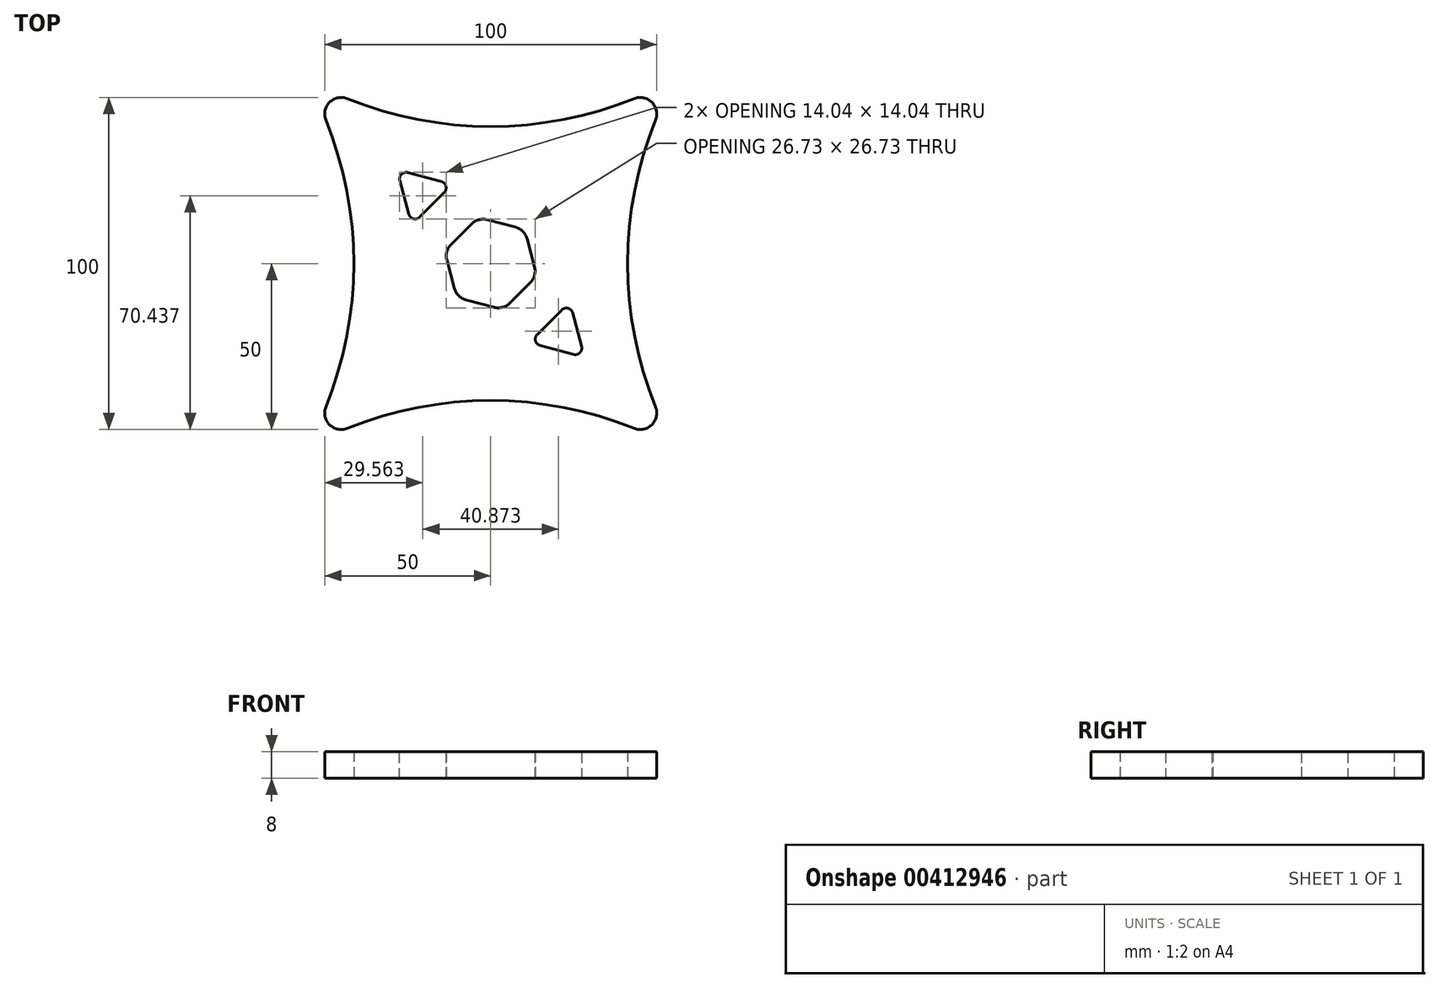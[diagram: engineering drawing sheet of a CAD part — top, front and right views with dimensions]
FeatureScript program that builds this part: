
annotation { "Feature Type Name" : "Feature", "Feature Type Description" : "" }
export const myFeature = defineFeature(function(context is Context, id is Id, definition is map)
    precondition{}
    {
        {
            var Q0;
            Q0=qCreatedBy(makeId("Top.planeOp"),FACE);
            var sketch = newSketch(context, id + "F0", { "sketchPlane" : qUnion([Q0])});
            skLineSegment(sketch, "E0.bottom", {"start": v(55.55, -55.55) * mm, "end": v(-55.55, -55.55) * mm, "construction": true});
            skLineSegment(sketch, "E0.top", {"start": v(55.55, 55.55) * mm, "end": v(-55.55, 55.55) * mm, "construction": true});
            skLineSegment(sketch, "E0.left", {"start": v(55.55, -55.55) * mm, "end": v(55.55, 55.55) * mm, "construction": true});
            skLineSegment(sketch, "E0.right", {"start": v(-55.55, -55.55) * mm, "end": v(-55.55, 55.55) * mm, "construction": true});
            skArc(sketch, "E1", {"start": v(-43.13, 49.64) * mm, "mid": v(0, 41.24) * mm, "end": v(43.12, 49.64) * mm});
            skArc(sketch, "E2.MirrorCS", {"start": v(-43.13, -49.64) * mm, "mid": v(0, -41.24) * mm, "end": v(43.12, -49.64) * mm});
            skArc(sketch, "E3", {"start": v(-49.64, -43.12) * mm, "mid": v(-41.24, 0) * mm, "end": v(-49.64, 43.12) * mm});
            skArc(sketch, "E4.MirrorCS", {"start": v(49.64, -43.12) * mm, "mid": v(41.24, 0) * mm, "end": v(49.64, 43.12) * mm});
            skPoint(sketch, "E5.visualSharp", {"position": v(-55.55, 55.55) * mm});
            skArc(sketch, "E5.filletArc", {"start": v(-43.12, 49.64) * mm, "mid": v(-48.54, 48.54) * mm, "end": v(-49.64, 43.12) * mm});
            skPoint(sketch, "E6.visualSharp", {"position": v(55.55, 55.55) * mm});
            skArc(sketch, "E6.filletArc", {"start": v(49.64, 43.12) * mm, "mid": v(48.54, 48.54) * mm, "end": v(43.12, 49.64) * mm});
            skPoint(sketch, "E7.visualSharp", {"position": v(55.55, -55.55) * mm});
            skArc(sketch, "E7.filletArc", {"start": v(43.12, -49.64) * mm, "mid": v(48.54, -48.54) * mm, "end": v(49.64, -43.12) * mm});
            skPoint(sketch, "E8.visualSharp", {"position": v(-55.55, -55.55) * mm});
            skArc(sketch, "E8.filletArc", {"start": v(-49.64, -43.12) * mm, "mid": v(-48.54, -48.54) * mm, "end": v(-43.12, -49.64) * mm});
            skLineSegment(sketch, "E9", {"start": v(55.55, 55.55) * mm, "end": v(-55.55, -55.55) * mm, "construction": true});
            skLineSegment(sketch, "E10", {"start": v(-55.55, 55.55) * mm, "end": v(55.55, -55.55) * mm, "construction": true});
            skCircle(sketch, "E11.cCircle", {"center": v(0, 0) * mm, "radius": 12.5 * mm, "construction": true});
            skLineSegment(sketch, "E11.0", {"start": v(11.9, -5.78) * mm, "end": v(5.78, -11.9) * mm});
            skLineSegment(sketch, "E11.1", {"start": v(0.95, -13.2) * mm, "end": v(-7.42, -10.95) * mm});
            skLineSegment(sketch, "E11.2", {"start": v(-10.95, -7.42) * mm, "end": v(-13.2, 0.95) * mm});
            skLineSegment(sketch, "E11.3", {"start": v(-11.9, 5.78) * mm, "end": v(-5.78, 11.9) * mm});
            skLineSegment(sketch, "E11.4", {"start": v(-0.95, 13.2) * mm, "end": v(7.42, 10.95) * mm});
            skLineSegment(sketch, "E11.5", {"start": v(10.95, 7.42) * mm, "end": v(13.2, -0.95) * mm});
            skPoint(sketch, "E11.0.midPoint", {"position": v(8.84, -8.84) * mm});
            skPoint(sketch, "E12.visualSharp", {"position": v(-3.74, 13.94) * mm});
            skArc(sketch, "E12.filletArc", {"start": v(-0.95, 13.2) * mm, "mid": v(-3.54, 13.2) * mm, "end": v(-5.78, 11.9) * mm});
            skPoint(sketch, "E13.visualSharp", {"position": v(-13.94, 3.74) * mm});
            skArc(sketch, "E13.filletArc", {"start": v(-11.9, 5.78) * mm, "mid": v(-13.2, 3.54) * mm, "end": v(-13.2, 0.95) * mm});
            skPoint(sketch, "E14.visualSharp", {"position": v(-10.2, -10.2) * mm});
            skArc(sketch, "E14.filletArc", {"start": v(-10.95, -7.42) * mm, "mid": v(-9.66, -9.66) * mm, "end": v(-7.42, -10.95) * mm});
            skPoint(sketch, "E15.visualSharp", {"position": v(3.74, -13.94) * mm});
            skArc(sketch, "E15.filletArc", {"start": v(0.95, -13.2) * mm, "mid": v(3.54, -13.2) * mm, "end": v(5.78, -11.9) * mm});
            skPoint(sketch, "E16.visualSharp", {"position": v(13.94, -3.74) * mm});
            skArc(sketch, "E16.filletArc", {"start": v(11.9, -5.78) * mm, "mid": v(13.2, -3.54) * mm, "end": v(13.2, -0.95) * mm});
            skPoint(sketch, "E17.visualSharp", {"position": v(10.2, 10.2) * mm});
            skArc(sketch, "E17.filletArc", {"start": v(10.95, 7.42) * mm, "mid": v(9.66, 9.66) * mm, "end": v(7.42, 10.95) * mm});
            skCircle(sketch, "E18.cCircle", {"center": v(-21.21, 21.21) * mm, "radius": 5 * mm, "construction": true});
            skLineSegment(sketch, "E18.0", {"start": v(-11.55, 23.8) * mm, "end": v(-23.8, 11.55) * mm});
            skLineSegment(sketch, "E18.1", {"start": v(-23.8, 11.55) * mm, "end": v(-28.28, 28.28) * mm});
            skLineSegment(sketch, "E18.2", {"start": v(-28.28, 28.28) * mm, "end": v(-11.55, 23.8) * mm});
            skPoint(sketch, "E18.0.midPoint", {"position": v(-17.68, 17.68) * mm});
            skLineSegment(sketch, "E19.MirrorCS", {"start": v(28.28, -28.28) * mm, "end": v(23.8, -11.55) * mm});
            skLineSegment(sketch, "E20.MirrorCS", {"start": v(23.8, -11.55) * mm, "end": v(11.55, -23.8) * mm});
            skLineSegment(sketch, "E21.MirrorCS", {"start": v(11.55, -23.8) * mm, "end": v(28.28, -28.28) * mm});
            skCircle(sketch, "E22.MirrorC", {"center": v(21.21, -21.21) * mm, "radius": 5 * mm, "construction": true});
            skSolve(sketch);
        }
        {
            var Q0;
            Q0 = qSketchRegion(id + "F0", true);
            extrude(context, id + "F1", {"entities" : qUnion([Q0]), "depth" : 8 * mm});
        }
        {
            var Q0;
            Q0=makeQuery(id+"F1.opExtrude","SWEPT_EDGE",EDGE,{"disambiguationData":[OSD([sQuery(id+"F0.wireOp",EDGE,"E18.1"),sQuery(id+"F0.wireOp",EDGE,"E18.2")])]});
            var Q1;
            Q1=makeQuery(id+"F1.opExtrude","SWEPT_EDGE",EDGE,{"disambiguationData":[OSD([sQuery(id+"F0.wireOp",EDGE,"E18.0"),sQuery(id+"F0.wireOp",EDGE,"E18.2")])]});
            var Q2;
            Q2=makeQuery(id+"F1.opExtrude","SWEPT_EDGE",EDGE,{"disambiguationData":[OSD([sQuery(id+"F0.wireOp",EDGE,"E18.0"),sQuery(id+"F0.wireOp",EDGE,"E18.1")])]});
            var Q3;
            Q3=makeQuery(id+"F1.opExtrude","SWEPT_EDGE",EDGE,{"disambiguationData":[OSD([sQuery(id+"F0.wireOp",EDGE,"E19.MirrorCS"),sQuery(id+"F0.wireOp",EDGE,"E20.MirrorCS")])]});
            var Q4;
            Q4=makeQuery(id+"F1.opExtrude","SWEPT_EDGE",EDGE,{"disambiguationData":[OSD([sQuery(id+"F0.wireOp",EDGE,"E20.MirrorCS"),sQuery(id+"F0.wireOp",EDGE,"E21.MirrorCS")])]});
            var Q5;
            Q5=makeQuery(id+"F1.opExtrude","SWEPT_EDGE",EDGE,{"disambiguationData":[OSD([sQuery(id+"F0.wireOp",EDGE,"E19.MirrorCS"),sQuery(id+"F0.wireOp",EDGE,"E21.MirrorCS")])]});
            fillet(context, id + "F2", {"entities" : qUnion([Q0, Q1, Q2, Q3, Q4, Q5]), "radius" : 2 * mm, "tangentPropagation" : true, "allowEdgeOverflow" : false});
        }
    });
